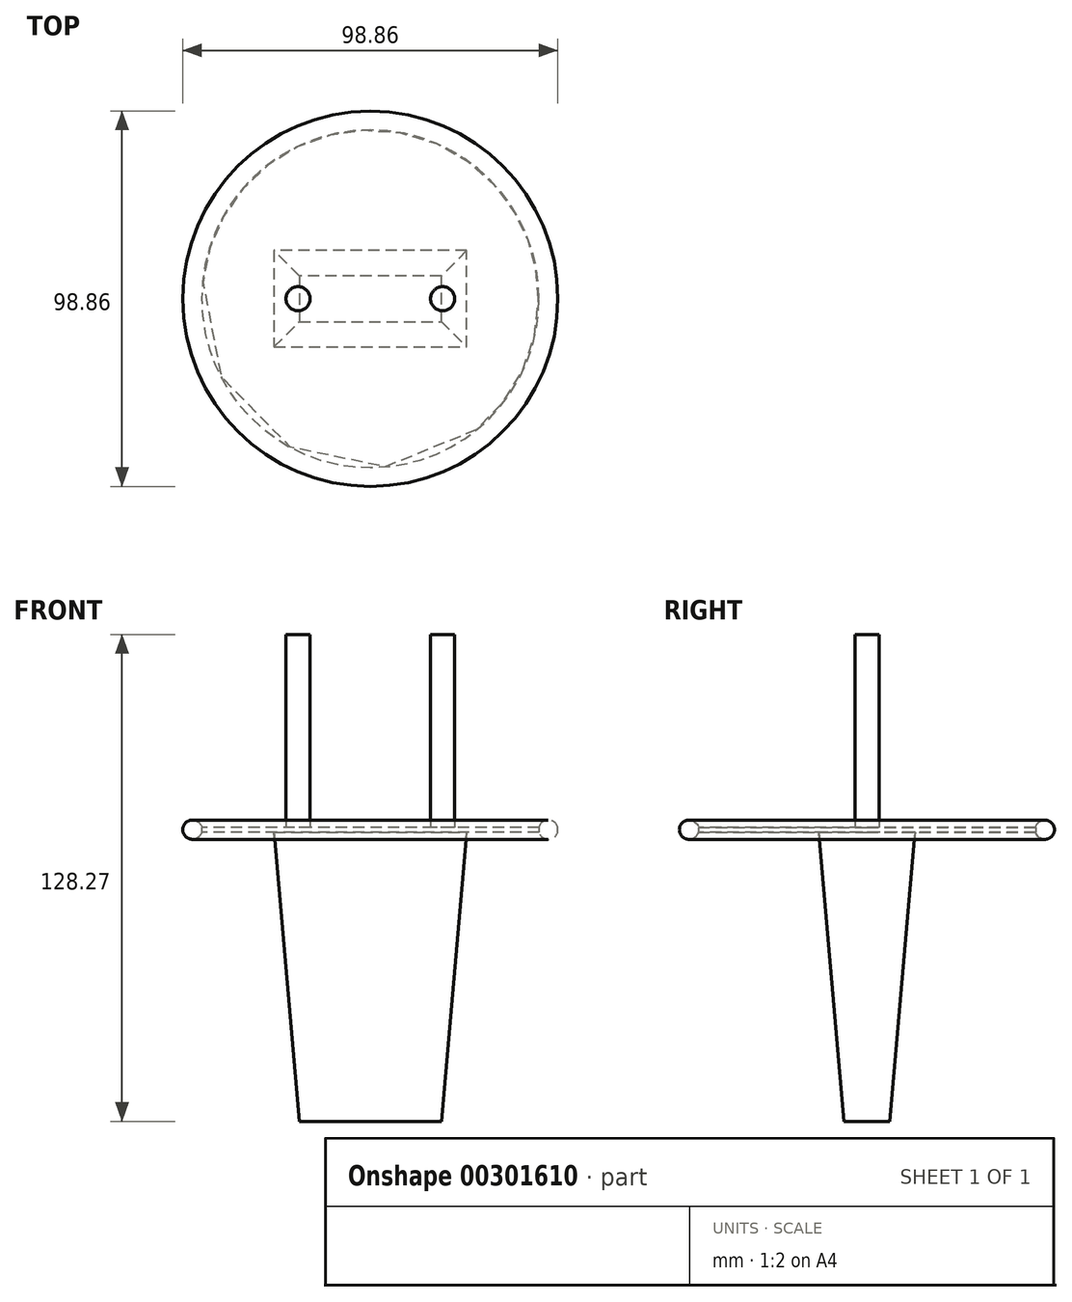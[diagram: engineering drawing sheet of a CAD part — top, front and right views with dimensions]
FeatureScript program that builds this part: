
annotation { "Feature Type Name" : "Feature", "Feature Type Description" : "" }
export const myFeature = defineFeature(function(context is Context, id is Id, definition is map)
    precondition{}
    {
        {
            var Q0;
            Q0=qCreatedBy(makeId("Top.planeOp"),FACE);
            var sketch = newSketch(context, id + "F0", { "sketchPlane" : qUnion([Q0])});
            skCircle(sketch, "E0", {"center": v(0, 0) * mm, "radius": 44.45 * mm});
            skSolve(sketch);
        }
        {
            var Q0;
            Q0 = qSketchRegion(id + "F0", true);
            extrude(context, id + "F1", {"entities" : qUnion([Q0]), "endBound" : BoundingType.SYMMETRIC, "depth" : 1.27 * mm});
        }
        {
            var Q0;
            Q0=qCreatedBy(makeId("Top.planeOp"),FACE);
            var sketch = newSketch(context, id + "F2", { "sketchPlane" : qUnion([Q0])});
            skCircle(sketch, "E1.0", {"center": v(0, 0) * mm, "radius": 48.26 * mm});
            skSolve(sketch);
        }
        {
            var Q0;
            Q0=qCreatedBy(makeId("Front.planeOp"),FACE);
            var sketch = newSketch(context, id + "F3", { "sketchPlane" : qUnion([Q0])});
            skCircle(sketch, "E2", {"center": v(-46.89, 0) * mm, "radius": 2.54 * mm});
            skSolve(sketch);
        }
        {
            var Q0;
            Q0=makeQuery(id+"F3.imprint","IMPRINT",FACE,{"disambiguationData":[TD([[makeQuery(id+"F3.imprint","IMPRINT",EDGE,{"derivedFrom":sQuery(id+"F3.wireOp",EDGE,"E2")}),1.0]])]});
            var Q1;
            Q1=sQuery(id+"F2.wireOp",EDGE,"E1.0");
            sweep(context, id + "F4", {"profiles" : qUnion([Q0]), "path" : qUnion([Q1])});
        }
        {
            var Q0;
            Q0=makeQuery(id+"F1.opExtrude","CAP_FACE",FACE,{"disambiguationData":[OSD([sQuery(id+"F0.wireOp",EDGE,"E0")])],"isStart":true});
            var sketch = newSketch(context, id + "F5", { "sketchPlane" : qUnion([Q0])});
            skLineSegment(sketch, "E3.bottom", {"start": v(-25.4, 12.7) * mm, "end": v(25.4, 12.7) * mm});
            skLineSegment(sketch, "E3.top", {"start": v(-25.4, -12.7) * mm, "end": v(25.4, -12.7) * mm});
            skLineSegment(sketch, "E3.left", {"start": v(-25.4, 12.7) * mm, "end": v(-25.4, -12.7) * mm});
            skLineSegment(sketch, "E3.right", {"start": v(25.4, 12.7) * mm, "end": v(25.4, -12.7) * mm});
            skSolve(sketch);
        }
        {
            var Q0;
            Q0 = qSketchRegion(id + "F5", true);
            extrude(context, id + "F6", {"entities" : qUnion([Q0]), "depth" : 76.2 * mm, "hasDraft" : true, "draftAngle" : 5 * degree, "draftPullDirection" : true});
        }
        {
            var Q0;
            Q0=makeQuery(id+"F1.opExtrude","CAP_FACE",FACE,{"disambiguationData":[OSD([sQuery(id+"F0.wireOp",EDGE,"E0")])],"isStart":false});
            var sketch = newSketch(context, id + "F7", { "sketchPlane" : qUnion([Q0])});
            skCircle(sketch, "E4", {"center": v(-19.05, 0) * mm, "radius": 3.18 * mm});
            skCircle(sketch, "E5", {"center": v(19.05, 0) * mm, "radius": 3.18 * mm});
            skSolve(sketch);
        }
        {
            var Q0;
            Q0=makeQuery(id+"F7.imprint","IMPRINT",FACE,{"disambiguationData":[TD([[makeQuery(id+"F7.imprint","IMPRINT",EDGE,{"derivedFrom":sQuery(id+"F7.wireOp",EDGE,"E4")}),-1.0]])]});
            cPlane(context, id + "F8", {"entities" : qUnion([Q0]), "cplaneType" : CPlaneType.OFFSET, "offset" : 50.8 * mm, "width" : 152.4 * mm, "height" : 152.4 * mm});
        }
        {
            var Q0;
            Q0 = qSketchRegion(id + "F7", true);
            var Q1;
            Q1=qCreatedBy(id+"F8.planeOp",FACE);
            extrude(context, id + "F9", {"entities" : qUnion([Q0]), "operationType" : NewBodyOperationType.ADD, "endBound" : BoundingType.UP_TO_SURFACE, "endBoundEntityFace" : qUnion([Q1]), "depth" : 25.4 * mm});
        }
    });
